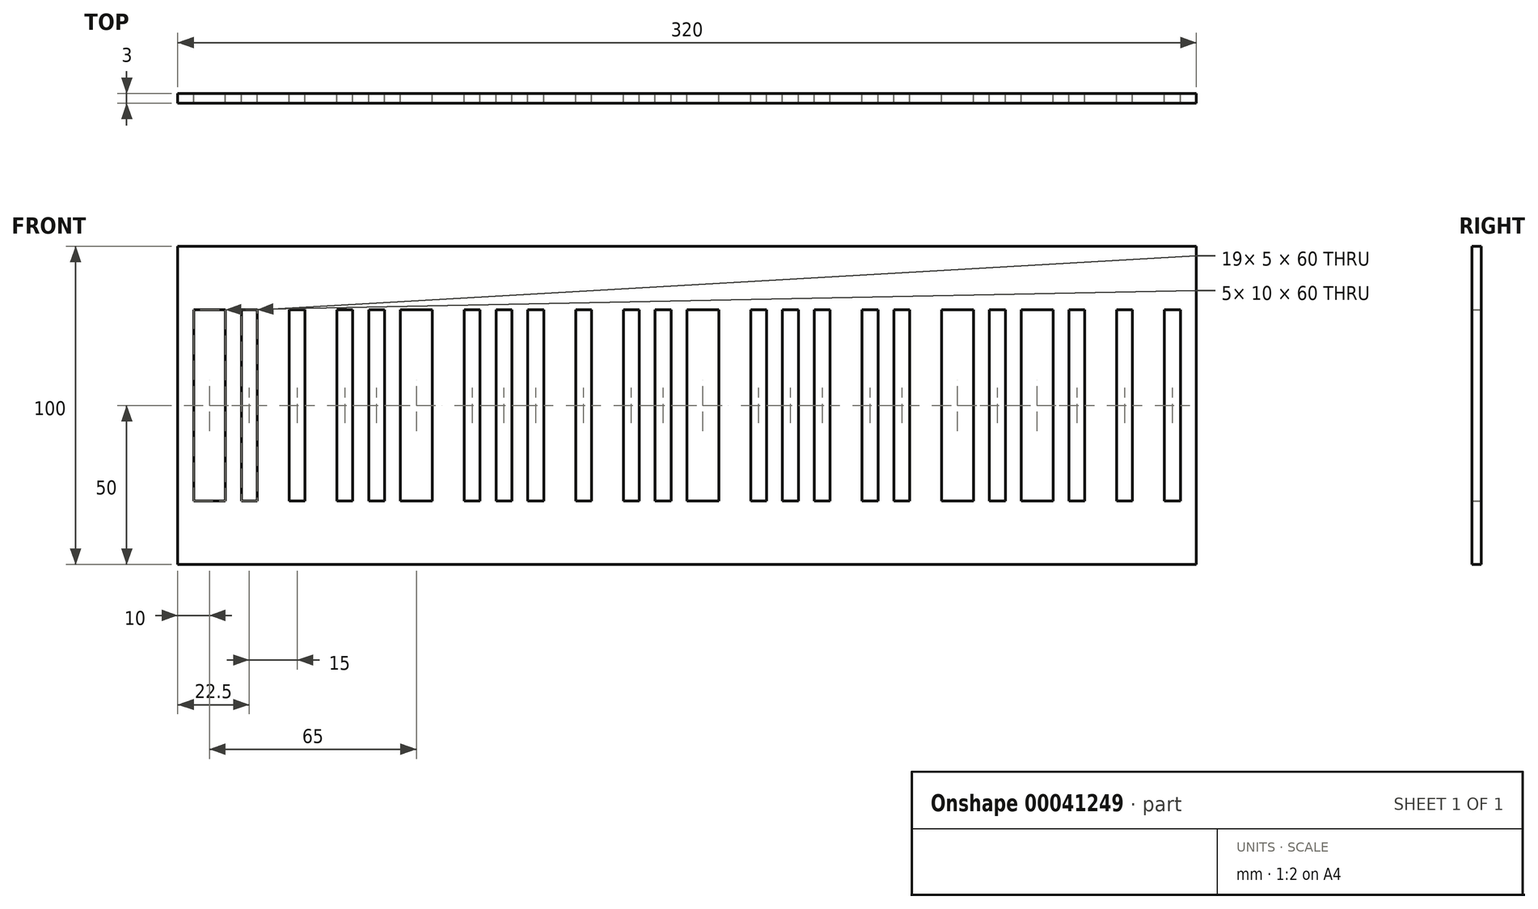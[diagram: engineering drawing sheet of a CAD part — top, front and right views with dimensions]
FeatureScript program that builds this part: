
annotation { "Feature Type Name" : "Feature", "Feature Type Description" : "" }
export const myFeature = defineFeature(function(context is Context, id is Id, definition is map)
    precondition{}
    {
        {
            var Q0;
            Q0=qCreatedBy(makeId("Front.planeOp"),FACE);
            var sketch = newSketch(context, id + "F0", { "sketchPlane" : qUnion([Q0])});
            skLineSegment(sketch, "E0", {"start": v(-75, -20) * mm, "end": v(75, -20) * mm, "construction": true});
            skPoint(sketch, "E1", {"position": v(0, -80) * mm});
            skPoint(sketch, "E2.1.0.0", {"position": v(5, -80) * mm});
            skPoint(sketch, "E2.2.0.0", {"position": v(10, -80) * mm});
            skPoint(sketch, "E2.3.0.0", {"position": v(15, -80) * mm});
            skPoint(sketch, "E2.4.0.0", {"position": v(20, -80) * mm});
            skPoint(sketch, "E2.5.0.0", {"position": v(25, -80) * mm});
            skPoint(sketch, "E2.6.0.0", {"position": v(30, -80) * mm});
            skPoint(sketch, "E2.7.0.0", {"position": v(35, -80) * mm});
            skPoint(sketch, "E2.8.0.0", {"position": v(40, -80) * mm});
            skPoint(sketch, "E2.9.0.0", {"position": v(45, -80) * mm});
            skPoint(sketch, "E2.10.0.0", {"position": v(50, -80) * mm});
            skPoint(sketch, "E2.11.0.0", {"position": v(55, -80) * mm});
            skLineSegment(sketch, "E2.direction1", {"start": v(0, -80) * mm, "end": v(5, -80) * mm, "construction": true});
            skPoint(sketch, "E3.0.12.0", {"position": v(60, -80) * mm});
            skPoint(sketch, "E3.0.13.0", {"position": v(65, -80) * mm});
            skPoint(sketch, "E3.0.14.0", {"position": v(70, -80) * mm});
            skPoint(sketch, "E3.0.15.0", {"position": v(75, -80) * mm});
            skPoint(sketch, "E3.0.16.0", {"position": v(80, -80) * mm});
            skPoint(sketch, "E3.0.17.0", {"position": v(85, -80) * mm});
            skPoint(sketch, "E3.0.18.0", {"position": v(90, -80) * mm});
            skPoint(sketch, "E3.0.19.0", {"position": v(95, -80) * mm});
            skPoint(sketch, "E3.0.20.0", {"position": v(100, -80) * mm});
            skPoint(sketch, "E3.0.21.0", {"position": v(105, -80) * mm});
            skPoint(sketch, "E3.0.22.0", {"position": v(110, -80) * mm});
            skPoint(sketch, "E3.0.23.0", {"position": v(115, -80) * mm});
            skPoint(sketch, "E3.0.24.0", {"position": v(120, -80) * mm});
            skPoint(sketch, "E3.0.25.0", {"position": v(125, -80) * mm});
            skPoint(sketch, "E3.0.26.0", {"position": v(130, -80) * mm});
            skPoint(sketch, "E3.0.27.0", {"position": v(135, -80) * mm});
            skPoint(sketch, "E3.0.28.0", {"position": v(140, -80) * mm});
            skPoint(sketch, "E3.0.29.0", {"position": v(145, -80) * mm});
            skPoint(sketch, "E3.0.30.0", {"position": v(150, -80) * mm});
            skPoint(sketch, "E3.0.31.0", {"position": v(155, -80) * mm});
            skPoint(sketch, "E3.0.32.0", {"position": v(160, -80) * mm});
            skPoint(sketch, "E3.0.33.0", {"position": v(165, -80) * mm});
            skPoint(sketch, "E3.0.34.0", {"position": v(170, -80) * mm});
            skPoint(sketch, "E3.0.35.0", {"position": v(175, -80) * mm});
            skPoint(sketch, "E3.0.36.0", {"position": v(180, -80) * mm});
            skPoint(sketch, "E3.0.37.0", {"position": v(185, -80) * mm});
            skPoint(sketch, "E3.0.38.0", {"position": v(190, -80) * mm});
            skPoint(sketch, "E3.0.39.0", {"position": v(195, -80) * mm});
            skPoint(sketch, "E3.0.40.0", {"position": v(200, -80) * mm});
            skPoint(sketch, "E3.0.41.0", {"position": v(205, -80) * mm});
            skPoint(sketch, "E3.0.42.0", {"position": v(210, -80) * mm});
            skPoint(sketch, "E3.0.43.0", {"position": v(215, -80) * mm});
            skPoint(sketch, "E3.0.44.0", {"position": v(220, -80) * mm});
            skPoint(sketch, "E3.0.45.0", {"position": v(225, -80) * mm});
            skPoint(sketch, "E3.0.46.0", {"position": v(230, -80) * mm});
            skPoint(sketch, "E3.0.47.0", {"position": v(235, -80) * mm});
            skPoint(sketch, "E3.0.48.0", {"position": v(240, -80) * mm});
            skPoint(sketch, "E3.0.49.0", {"position": v(245, -80) * mm});
            skPoint(sketch, "E3.0.50.0", {"position": v(250, -80) * mm});
            skPoint(sketch, "E3.0.51.0", {"position": v(255, -80) * mm});
            skPoint(sketch, "E3.0.52.0", {"position": v(260, -80) * mm});
            skPoint(sketch, "E3.0.53.0", {"position": v(265, -80) * mm});
            skPoint(sketch, "E3.0.54.0", {"position": v(270, -80) * mm});
            skPoint(sketch, "E3.0.55.0", {"position": v(275, -80) * mm});
            skPoint(sketch, "E3.0.56.0", {"position": v(280, -80) * mm});
            skPoint(sketch, "E3.0.57.0", {"position": v(285, -80) * mm});
            skPoint(sketch, "E3.0.58.0", {"position": v(290, -80) * mm});
            skPoint(sketch, "E3.0.59.0", {"position": v(295, -80) * mm});
            skLineSegment(sketch, "E4.bottom", {"start": v(5, -80) * mm, "end": v(15, -80) * mm});
            skLineSegment(sketch, "E4.top", {"start": v(5, -20) * mm, "end": v(15, -20) * mm});
            skLineSegment(sketch, "E4.left", {"start": v(5, -20) * mm, "end": v(5, -80) * mm});
            skLineSegment(sketch, "E4.right", {"start": v(15, -20) * mm, "end": v(15, -80) * mm});
            skLineSegment(sketch, "E5.bottom", {"start": v(20, -80) * mm, "end": v(25, -80) * mm});
            skLineSegment(sketch, "E5.top", {"start": v(20, -20) * mm, "end": v(25, -20) * mm});
            skLineSegment(sketch, "E5.left", {"start": v(20, -20) * mm, "end": v(20, -80) * mm});
            skLineSegment(sketch, "E5.right", {"start": v(25, -20) * mm, "end": v(25, -80) * mm});
            skLineSegment(sketch, "E6.bottom", {"start": v(35, -80) * mm, "end": v(40, -80) * mm});
            skLineSegment(sketch, "E6.top", {"start": v(35, -20) * mm, "end": v(40, -20) * mm});
            skLineSegment(sketch, "E6.left", {"start": v(35, -20) * mm, "end": v(35, -80) * mm});
            skLineSegment(sketch, "E6.right", {"start": v(40, -20) * mm, "end": v(40, -80) * mm});
            skLineSegment(sketch, "E7.bottom", {"start": v(50, -80) * mm, "end": v(55, -80) * mm});
            skLineSegment(sketch, "E7.top", {"start": v(50, -20) * mm, "end": v(55, -20) * mm});
            skLineSegment(sketch, "E7.left", {"start": v(50, -20) * mm, "end": v(50, -80) * mm});
            skLineSegment(sketch, "E7.right", {"start": v(55, -20) * mm, "end": v(55, -80) * mm});
            skLineSegment(sketch, "E8.bottom", {"start": v(60, -80) * mm, "end": v(65, -80) * mm});
            skLineSegment(sketch, "E8.top", {"start": v(60, -20) * mm, "end": v(65, -20) * mm});
            skLineSegment(sketch, "E8.left", {"start": v(60, -20) * mm, "end": v(60, -80) * mm});
            skLineSegment(sketch, "E8.right", {"start": v(65, -20) * mm, "end": v(65, -80) * mm});
            skLineSegment(sketch, "E9.bottom", {"start": v(70, -80) * mm, "end": v(80, -80) * mm});
            skLineSegment(sketch, "E9.top", {"start": v(70, -20) * mm, "end": v(80, -20) * mm});
            skLineSegment(sketch, "E9.left", {"start": v(70, -20) * mm, "end": v(70, -80) * mm});
            skLineSegment(sketch, "E9.right", {"start": v(80, -20) * mm, "end": v(80, -80) * mm});
            skLineSegment(sketch, "E10.bottom", {"start": v(90, -80) * mm, "end": v(95, -80) * mm});
            skLineSegment(sketch, "E10.top", {"start": v(90, -20) * mm, "end": v(95, -20) * mm});
            skLineSegment(sketch, "E10.left", {"start": v(90, -20) * mm, "end": v(90, -80) * mm});
            skLineSegment(sketch, "E10.right", {"start": v(95, -20) * mm, "end": v(95, -80) * mm});
            skLineSegment(sketch, "E11.bottom", {"start": v(100, -80) * mm, "end": v(105, -80) * mm});
            skLineSegment(sketch, "E11.top", {"start": v(100, -20) * mm, "end": v(105, -20) * mm});
            skLineSegment(sketch, "E11.left", {"start": v(100, -20) * mm, "end": v(100, -80) * mm});
            skLineSegment(sketch, "E11.right", {"start": v(105, -20) * mm, "end": v(105, -80) * mm});
            skLineSegment(sketch, "E12.bottom", {"start": v(110, -80) * mm, "end": v(115, -80) * mm});
            skLineSegment(sketch, "E12.top", {"start": v(110, -20) * mm, "end": v(115, -20) * mm});
            skLineSegment(sketch, "E12.left", {"start": v(110, -20) * mm, "end": v(110, -80) * mm});
            skLineSegment(sketch, "E12.right", {"start": v(115, -20) * mm, "end": v(115, -80) * mm});
            skLineSegment(sketch, "E13.bottom", {"start": v(125, -80) * mm, "end": v(130, -80) * mm});
            skLineSegment(sketch, "E13.top", {"start": v(125, -20) * mm, "end": v(130, -20) * mm});
            skLineSegment(sketch, "E13.left", {"start": v(125, -20) * mm, "end": v(125, -80) * mm});
            skLineSegment(sketch, "E13.right", {"start": v(130, -20) * mm, "end": v(130, -80) * mm});
            skLineSegment(sketch, "E14.bottom", {"start": v(140, -80) * mm, "end": v(145, -80) * mm});
            skLineSegment(sketch, "E14.top", {"start": v(140, -20) * mm, "end": v(145, -20) * mm});
            skLineSegment(sketch, "E14.left", {"start": v(140, -20) * mm, "end": v(140, -80) * mm});
            skLineSegment(sketch, "E14.right", {"start": v(145, -20) * mm, "end": v(145, -80) * mm});
            skLineSegment(sketch, "E15.bottom", {"start": v(150, -80) * mm, "end": v(155, -80) * mm});
            skLineSegment(sketch, "E15.top", {"start": v(150, -20) * mm, "end": v(155, -20) * mm});
            skLineSegment(sketch, "E15.left", {"start": v(150, -20) * mm, "end": v(150, -80) * mm});
            skLineSegment(sketch, "E15.right", {"start": v(155, -20) * mm, "end": v(155, -80) * mm});
            skLineSegment(sketch, "E16.bottom", {"start": v(160, -80) * mm, "end": v(170, -80) * mm});
            skLineSegment(sketch, "E16.top", {"start": v(160, -20) * mm, "end": v(170, -20) * mm});
            skLineSegment(sketch, "E16.left", {"start": v(160, -20) * mm, "end": v(160, -80) * mm});
            skLineSegment(sketch, "E16.right", {"start": v(170, -20) * mm, "end": v(170, -80) * mm});
            skLineSegment(sketch, "E17.bottom", {"start": v(180, -80) * mm, "end": v(185, -80) * mm});
            skLineSegment(sketch, "E17.top", {"start": v(180, -20) * mm, "end": v(185, -20) * mm});
            skLineSegment(sketch, "E17.left", {"start": v(180, -20) * mm, "end": v(180, -80) * mm});
            skLineSegment(sketch, "E17.right", {"start": v(185, -20) * mm, "end": v(185, -80) * mm});
            skLineSegment(sketch, "E18.bottom", {"start": v(190, -80) * mm, "end": v(195, -80) * mm});
            skLineSegment(sketch, "E18.top", {"start": v(190, -20) * mm, "end": v(195, -20) * mm});
            skLineSegment(sketch, "E18.left", {"start": v(190, -20) * mm, "end": v(190, -80) * mm});
            skLineSegment(sketch, "E18.right", {"start": v(195, -20) * mm, "end": v(195, -80) * mm});
            skLineSegment(sketch, "E19.bottom", {"start": v(200, -80) * mm, "end": v(205, -80) * mm});
            skLineSegment(sketch, "E19.top", {"start": v(200, -20) * mm, "end": v(205, -20) * mm});
            skLineSegment(sketch, "E19.left", {"start": v(200, -20) * mm, "end": v(200, -80) * mm});
            skLineSegment(sketch, "E19.right", {"start": v(205, -20) * mm, "end": v(205, -80) * mm});
            skLineSegment(sketch, "E20.bottom", {"start": v(215, -80) * mm, "end": v(220, -80) * mm});
            skLineSegment(sketch, "E20.top", {"start": v(215, -20) * mm, "end": v(220, -20) * mm});
            skLineSegment(sketch, "E20.left", {"start": v(215, -20) * mm, "end": v(215, -80) * mm});
            skLineSegment(sketch, "E20.right", {"start": v(220, -20) * mm, "end": v(220, -80) * mm});
            skLineSegment(sketch, "E21.bottom", {"start": v(225, -80) * mm, "end": v(230, -80) * mm});
            skLineSegment(sketch, "E21.top", {"start": v(225, -20) * mm, "end": v(230, -20) * mm});
            skLineSegment(sketch, "E21.left", {"start": v(225, -20) * mm, "end": v(225, -80) * mm});
            skLineSegment(sketch, "E21.right", {"start": v(230, -20) * mm, "end": v(230, -80) * mm});
            skLineSegment(sketch, "E22.bottom", {"start": v(240, -80) * mm, "end": v(250, -80) * mm});
            skLineSegment(sketch, "E22.top", {"start": v(240, -20) * mm, "end": v(250, -20) * mm});
            skLineSegment(sketch, "E22.left", {"start": v(240, -20) * mm, "end": v(240, -80) * mm});
            skLineSegment(sketch, "E22.right", {"start": v(250, -20) * mm, "end": v(250, -80) * mm});
            skLineSegment(sketch, "E23.bottom", {"start": v(255, -80) * mm, "end": v(260, -80) * mm});
            skLineSegment(sketch, "E23.top", {"start": v(255, -20) * mm, "end": v(260, -20) * mm});
            skLineSegment(sketch, "E23.left", {"start": v(255, -20) * mm, "end": v(255, -80) * mm});
            skLineSegment(sketch, "E23.right", {"start": v(260, -20) * mm, "end": v(260, -80) * mm});
            skLineSegment(sketch, "E24.bottom", {"start": v(265, -80) * mm, "end": v(275, -80) * mm});
            skLineSegment(sketch, "E24.top", {"start": v(265, -20) * mm, "end": v(275, -20) * mm});
            skLineSegment(sketch, "E24.left", {"start": v(265, -20) * mm, "end": v(265, -80) * mm});
            skLineSegment(sketch, "E24.right", {"start": v(275, -20) * mm, "end": v(275, -80) * mm});
            skLineSegment(sketch, "E25.bottom", {"start": v(280, -80) * mm, "end": v(285, -80) * mm});
            skLineSegment(sketch, "E25.top", {"start": v(280, -20) * mm, "end": v(285, -20) * mm});
            skLineSegment(sketch, "E25.left", {"start": v(280, -20) * mm, "end": v(280, -80) * mm});
            skLineSegment(sketch, "E25.right", {"start": v(285, -20) * mm, "end": v(285, -80) * mm});
            skPoint(sketch, "E26.0.60.0", {"position": v(300, -80) * mm});
            skPoint(sketch, "E26.0.61.0", {"position": v(305, -80) * mm});
            skPoint(sketch, "E26.0.62.0", {"position": v(310, -80) * mm});
            skPoint(sketch, "E26.0.63.0", {"position": v(315, -80) * mm});
            skLineSegment(sketch, "E27.bottom", {"start": v(295, -80) * mm, "end": v(300, -80) * mm});
            skLineSegment(sketch, "E27.top", {"start": v(295, -20) * mm, "end": v(300, -20) * mm});
            skLineSegment(sketch, "E27.left", {"start": v(295, -20) * mm, "end": v(295, -80) * mm});
            skLineSegment(sketch, "E27.right", {"start": v(300, -20) * mm, "end": v(300, -80) * mm});
            skLineSegment(sketch, "E28.bottom", {"start": v(310, -80) * mm, "end": v(315, -80) * mm});
            skLineSegment(sketch, "E28.top", {"start": v(310, -20) * mm, "end": v(315, -20) * mm});
            skLineSegment(sketch, "E28.left", {"start": v(310, -20) * mm, "end": v(310, -80) * mm});
            skLineSegment(sketch, "E28.right", {"start": v(315, -20) * mm, "end": v(315, -80) * mm});
            skPoint(sketch, "E29.0.64.0", {"position": v(320, -80) * mm});
            skLineSegment(sketch, "E30.bottom", {"start": v(0, 0) * mm, "end": v(320, 0) * mm});
            skLineSegment(sketch, "E30.top", {"start": v(0, -100) * mm, "end": v(320, -100) * mm});
            skLineSegment(sketch, "E30.left", {"start": v(0, 0) * mm, "end": v(0, -100) * mm});
            skLineSegment(sketch, "E30.right", {"start": v(320, 0) * mm, "end": v(320, -100) * mm});
            skSolve(sketch);
        }
        {
            var Q0;
            Q0=makeQuery(id+"F0.imprint","IMPRINT",FACE,{"disambiguationData":[TD([[makeQuery(id+"F0.imprint","IMPRINT",EDGE,{"derivedFrom":sQuery(id+"F0.wireOp",EDGE,"E4.bottom")}),-1.0]])]});
            extrude(context, id + "F1", {"entities" : qUnion([Q0]), "depth" : 3 * mm});
        }
    });
